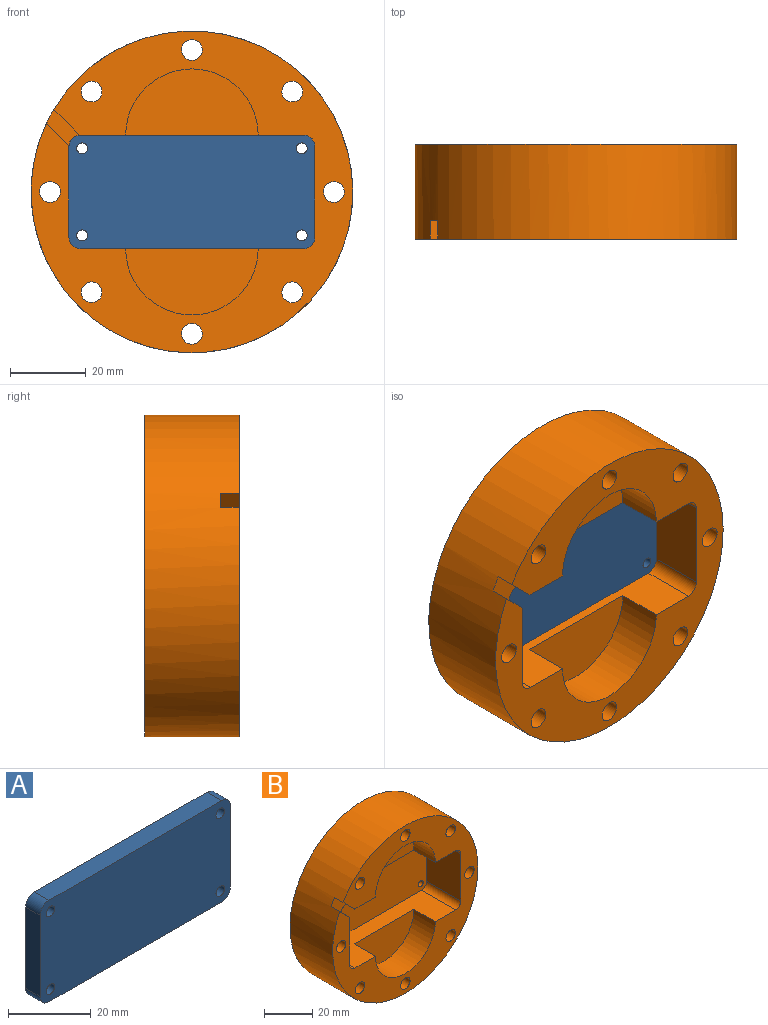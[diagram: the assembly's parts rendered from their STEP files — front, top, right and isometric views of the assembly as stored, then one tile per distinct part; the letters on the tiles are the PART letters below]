
ASSEMBLY  parts=2 mates=1
PART A: 14 faces, bbox 65x5x30 mm
  f0: plane 24x5mm, normal (1,0,0), area 120mm2, adj f4,f5,f10,f13
  f1: plane 59x5mm, normal (0,0,1), area 295mm2, adj f4,f5,f10,f11
  f2: plane 24x5mm, normal (-1,0,0), area 120mm2, adj f4,f5,f11,f12
  f3: plane 59x5mm, normal (0,0,-1), area 295mm2, adj f4,f5,f12,f13
  f4: plane 65x30mm, normal (0,-1,0), area 1915.9mm2, adj f0,f1,f2,f3,f6,f7,f8,f9
  f5: plane 65x30mm, normal (0,1,0), area 1915.9mm2, adj f0,f1,f2,f3,f6,f7,f8,f9
  f6: cylinder r=1.45mm len=5mm, axis (0,-1,0), area 45.6mm2, adj f4,f5
  f7: cylinder r=1.45mm len=5mm, axis (0,-1,0), area 45.6mm2, adj f4,f5
  f8: cylinder r=1.45mm len=5mm, axis (0,-1,0), area 45.6mm2, adj f4,f5
  f9: cylinder r=1.45mm len=5mm, axis (0,-1,0), area 45.6mm2, adj f4,f5
  f10: cylinder r=3mm len=5mm, axis (0,-1,0), area 23.6mm2, adj f0,f1,f4,f5
  f11: cylinder r=3mm len=5mm, axis (0,1,0), area 23.6mm2, adj f1,f2,f4,f5
  f12: cylinder r=3mm len=5mm, axis (0,-1,0), area 23.6mm2, adj f2,f3,f4,f5
  f13: cylinder r=3mm len=5mm, axis (0,1,0), area 23.6mm2, adj f0,f3,f4,f5
PART B: 31 faces, bbox 85x25x85 mm
  f0: plane 59x20mm, normal (0,0,1), area 742.5mm2, adj f1,f9,f10,f11,f27,f28
  f1: plane 85x85mm, normal (0,-1,0), area 2545.9mm2, adj f0,f2,f4,f5,f6,f7,f8,f9
  f2: cylinder r=42.5mm len=85mm, axis (0,1,0), area 6655mm2, adj f1,f3,f24,f25,f26
  f3: plane 85x85mm, normal (0,1,0), area 5458mm2, adj f2,f12,f13,f14,f15,f16,f17,f18
  f4: plane 24x20mm, normal (-1,0,0), area 480mm2, adj f1,f5,f10,f11
  f5: cylinder r=3mm len=20mm, axis (0,-1,0), area 94.2mm2, adj f1,f4,f6,f11
  f6: plane 59x20mm, normal (0,0,-1), area 742.5mm2, adj f1,f5,f7,f11,f29,f30
  f7: cylinder r=3mm len=20mm, axis (0,-1,0), area 72.4mm2, adj f1,f6,f8,f11,f24,f25,f26
  f8: plane 24x20mm, normal (1,0,0), area 480mm2, adj f1,f7,f9,f11
  f9: cylinder r=3mm len=20mm, axis (0,-1,0), area 94.2mm2, adj f0,f1,f8,f11
  f10: cylinder r=3mm len=20mm, axis (0,-1,0), area 94.2mm2, adj f0,f1,f4,f11
  f11: plane 65x30mm, normal (0,-1,0), area 1915.9mm2, adj f0,f4,f5,f6,f7,f8,f9,f10
  f12: cylinder r=1.45mm len=5mm, axis (0,-1,0), area 45.6mm2, adj f3,f11
  f13: cylinder r=1.45mm len=5mm, axis (0,-1,0), area 45.6mm2, adj f3,f11
  f14: cylinder r=1.45mm len=5mm, axis (0,-1,0), area 45.6mm2, adj f3,f11
  f15: cylinder r=1.45mm len=5mm, axis (0,-1,0), area 45.6mm2, adj f3,f11
  f16: cylinder r=2.75mm len=25mm, axis (0,-1,0), area 432mm2, adj f1,f3
  f17: cylinder r=2.75mm len=25mm, axis (0,-1,0), area 432mm2, adj f1,f3
  f18: cylinder r=2.75mm len=25mm, axis (0,-1,0), area 432mm2, adj f1,f3
  f19: cylinder r=2.75mm len=25mm, axis (0,-1,0), area 432mm2, adj f1,f3
  f20: cylinder r=2.75mm len=25mm, axis (0,-1,0), area 432mm2, adj f1,f3
  f21: cylinder r=2.75mm len=25mm, axis (0,-1,0), area 432mm2, adj f1,f3
  f22: cylinder r=2.75mm len=25mm, axis (0,-1,0), area 432mm2, adj f1,f3
  f23: cylinder r=2.75mm len=25mm, axis (0,-1,0), area 432mm2, adj f1,f3
  f24: plane 6.81x6.81mm, normal (-0.71,0,-0.71), area 48.2mm2, adj f1,f2,f7,f26
  f25: plane 5.95x5.95mm, normal (0.71,0,0.71), area 42.1mm2, adj f1,f2,f7,f26
  f26: plane 9.64x8.78mm, normal (0,-1,0), area 34.1mm2, adj f2,f7,f24,f25
  f27: cylinder r=17.5mm len=35mm, axis (0,-1,0), area 687.2mm2, adj f0,f1,f28
  f28: plane 35x17.5mm, normal (0,-1,0), area 481.1mm2, adj f0,f27
  f29: cylinder r=17.5mm len=35mm, axis (0,-1,0), area 687.2mm2, adj f1,f6,f30
  f30: plane 35x17.5mm, normal (0,-1,0), area 481.1mm2, adj f6,f29
PLACE A t=(-5.75,9.7,8.27)mm
PLACE B t=(-5.75,14.7,8.27)mm fixed
MATE parallel B.f2 <-> A.f5  axis (0,-1,0) through (-5.75,9.7,8.27)mm
